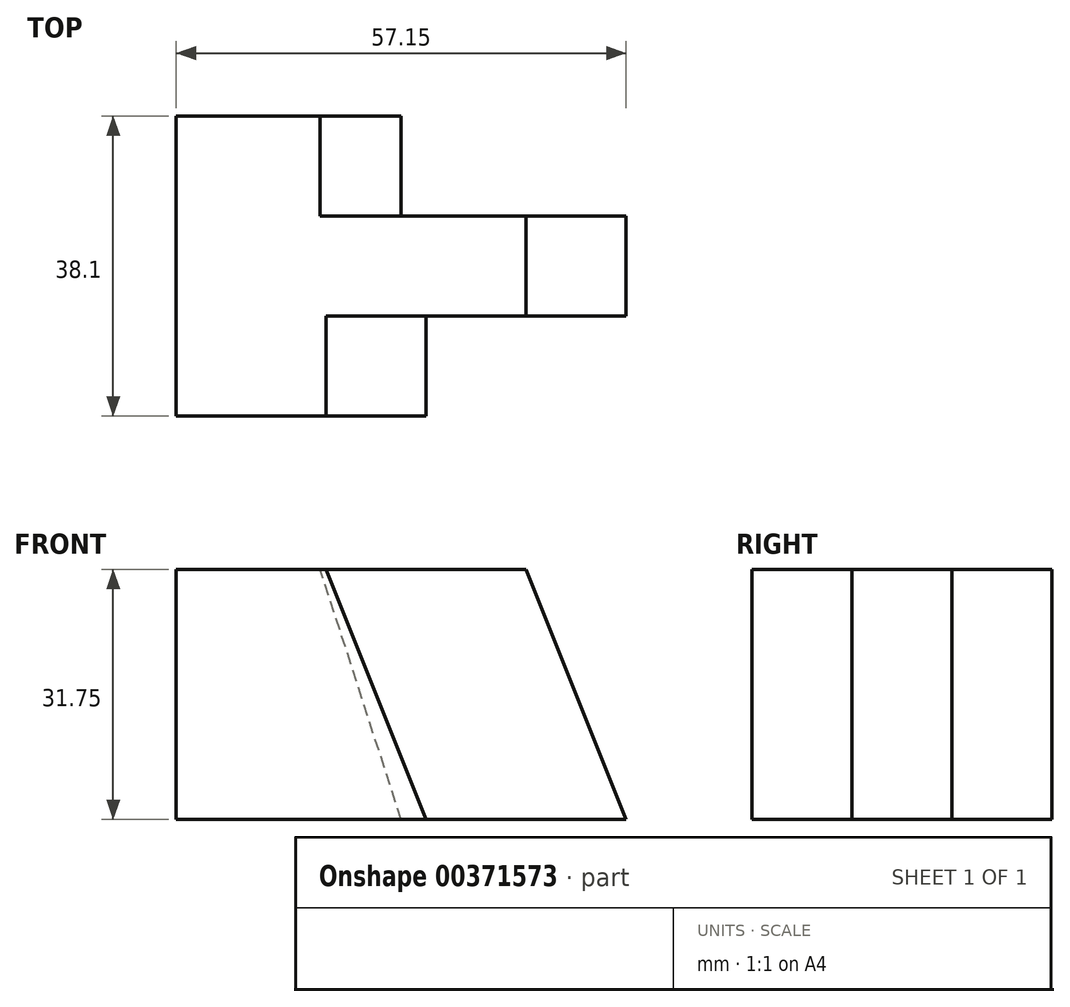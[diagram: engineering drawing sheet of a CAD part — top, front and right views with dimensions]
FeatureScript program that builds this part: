
annotation { "Feature Type Name" : "Feature", "Feature Type Description" : "" }
export const myFeature = defineFeature(function(context is Context, id is Id, definition is map)
    precondition{}
    {
        {
            var Q0;
            Q0=qCreatedBy(makeId("Front.planeOp"),FACE);
            var sketch = newSketch(context, id + "F0", { "sketchPlane" : qUnion([Q0])});
            skLineSegment(sketch, "E0", {"start": v(0, 0) * mm, "end": v(57.15, 0) * mm});
            skLineSegment(sketch, "E1", {"start": v(0, 0) * mm, "end": v(0, -31.75) * mm});
            skLineSegment(sketch, "E2", {"start": v(0, -31.75) * mm, "end": v(57.15, -31.75) * mm});
            skLineSegment(sketch, "E3", {"start": v(57.15, 0) * mm, "end": v(57.15, -31.75) * mm});
            skSolve(sketch);
        }
        {
            var Q0;
            Q0 = qSketchRegion(id + "F0", true);
            extrude(context, id + "F1", {"entities" : qUnion([Q0]), "depth" : 38.1 * mm});
        }
        {
            var Q0;
            Q0=makeQuery(id+"F1.opExtrude","CAP_FACE",FACE,{"disambiguationData":[OSD([sQuery(id+"F0.wireOp",EDGE,"E0"),sQuery(id+"F0.wireOp",EDGE,"E1"),sQuery(id+"F0.wireOp",EDGE,"E2"),sQuery(id+"F0.wireOp",EDGE,"E3")])],"isStart":false});
            var sketch = newSketch(context, id + "F2", { "sketchPlane" : qUnion([Q0])});
            skLineSegment(sketch, "E4", {"start": v(31.75, -31.75) * mm, "end": v(19.05, 0) * mm});
            skLineSegment(sketch, "E5", {"start": v(19.05, 0) * mm, "end": v(57.15, 0) * mm});
            skLineSegment(sketch, "E6", {"start": v(57.15, 0) * mm, "end": v(57.15, -31.75) * mm});
            skLineSegment(sketch, "E7", {"start": v(57.15, -31.75) * mm, "end": v(31.75, -31.75) * mm});
            skSolve(sketch);
        }
        {
            var Q0;
            Q0 = qSketchRegion(id + "F2", true);
            extrude(context, id + "F3", {"entities" : qUnion([Q0]), "operationType" : NewBodyOperationType.REMOVE, "oppositeDirection" : true, "depth" : 12.7 * mm});
        }
        {
            var Q0;
            Q0=makeQuery(id+"F1.opExtrude","CAP_FACE",FACE,{"disambiguationData":[OSD([sQuery(id+"F0.wireOp",EDGE,"E0"),sQuery(id+"F0.wireOp",EDGE,"E1"),sQuery(id+"F0.wireOp",EDGE,"E2"),sQuery(id+"F0.wireOp",EDGE,"E3")])],"isStart":true});
            var sketch = newSketch(context, id + "F4", { "sketchPlane" : qUnion([Q0])});
            skLineSegment(sketch, "E8", {"start": v(-28.58, -31.75) * mm, "end": v(-18.3, 0) * mm});
            skLineSegment(sketch, "E9", {"start": v(-18.3, 0) * mm, "end": v(-57.15, 0) * mm});
            skLineSegment(sketch, "E10", {"start": v(-57.15, 0) * mm, "end": v(-57.15, -31.75) * mm});
            skLineSegment(sketch, "E11", {"start": v(-57.15, -31.75) * mm, "end": v(-28.58, -31.75) * mm});
            skSolve(sketch);
        }
        {
            var Q0;
            Q0 = qSketchRegion(id + "F4", true);
            extrude(context, id + "F5", {"entities" : qUnion([Q0]), "operationType" : NewBodyOperationType.REMOVE, "oppositeDirection" : true, "depth" : 12.7 * mm});
        }
        {
            var Q0;
            Q0=makeQuery(id+"F5.boolean.opBoolean","COPY",FACE,{"derivedFrom":makeQuery(id+"F5.opExtrude","CAP_FACE",FACE,{"disambiguationData":[OSD([sQuery(id+"F4.wireOp",EDGE,"E8"),sQuery(id+"F4.wireOp",EDGE,"E9"),sQuery(id+"F4.wireOp",EDGE,"E10"),sQuery(id+"F4.wireOp",EDGE,"E11")])],"isStart":false})});
            var sketch = newSketch(context, id + "F6", { "sketchPlane" : qUnion([Q0])});
            skLineSegment(sketch, "E12", {"start": v(-44.45, 0) * mm, "end": v(-57.15, -31.75) * mm});
            skLineSegment(sketch, "E13", {"start": v(-57.15, -31.75) * mm, "end": v(-57.15, 0) * mm});
            skLineSegment(sketch, "E14", {"start": v(-57.15, 0) * mm, "end": v(-44.45, 0) * mm});
            skSolve(sketch);
        }
        {
            var Q0;
            Q0 = qSketchRegion(id + "F6", true);
            extrude(context, id + "F7", {"entities" : qUnion([Q0]), "operationType" : NewBodyOperationType.REMOVE, "oppositeDirection" : true, "depth" : 25.4 * mm});
        }
    });
